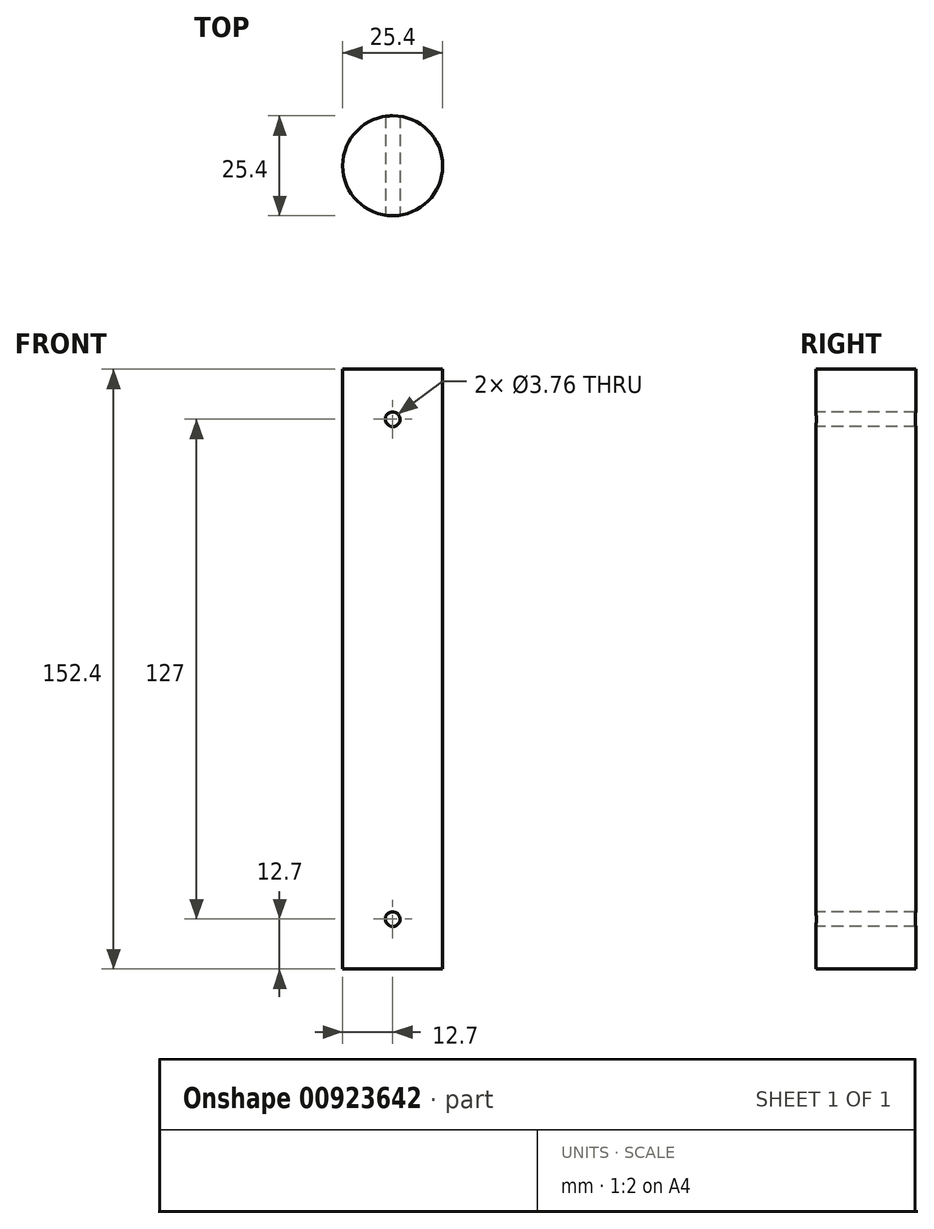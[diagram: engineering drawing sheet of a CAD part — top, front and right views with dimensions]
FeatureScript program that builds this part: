
annotation { "Feature Type Name" : "Feature", "Feature Type Description" : "" }
export const myFeature = defineFeature(function(context is Context, id is Id, definition is map)
    precondition{}
    {
        {
            var Q0;
            Q0=qCreatedBy(makeId("Top.planeOp"),FACE);
            var sketch = newSketch(context, id + "F0", { "sketchPlane" : qUnion([Q0])});
            skCircle(sketch, "E0", {"center": v(0, 0) * mm, "radius": 12.7 * mm});
            skSolve(sketch);
        }
        {
            var Q0;
            Q0=qSketchRegion(id+"F0",true);
            extrude(context, id + "F1", {"entities" : qUnion([Q0]), "depth" : 152.4 * mm});
        }
        {
            var Q0;
            Q0=qCreatedBy(makeId("Front.planeOp"),FACE);
            var sketch = newSketch(context, id + "F2", { "sketchPlane" : qUnion([Q0])});
            skCircle(sketch, "E1", {"center": v(0, 12.7) * mm, "radius": 1.88 * mm});
            skSolve(sketch);
        }
        {
            var Q0;
            Q0=qSketchRegion(id+"F2",true);
            extrude(context, id + "F3", {"entities" : qUnion([Q0]), "operationType" : NewBodyOperationType.REMOVE, "endBound" : BoundingType.SYMMETRIC, "oppositeDirection" : true, "depth" : 50.8 * mm});
        }
        {
            var Q0;
            Q0=qCreatedBy(makeId("Front.planeOp"),FACE);
            var sketch = newSketch(context, id + "F4", { "sketchPlane" : qUnion([Q0])});
            skLineSegment(sketch, "E2", {"start": v(0, 312.07) * mm, "end": v(0, 299.37) * mm});
            skCircle(sketch, "E3", {"center": v(0, 139.7) * mm, "radius": 1.88 * mm});
            skSolve(sketch);
        }
        {
            var Q0;
            Q0=qSketchRegion(id+"F4",true);
            extrude(context, id + "F5", {"entities" : qUnion([Q0]), "operationType" : NewBodyOperationType.REMOVE, "endBound" : BoundingType.SYMMETRIC, "oppositeDirection" : true, "depth" : 50.8 * mm});
        }
    });
